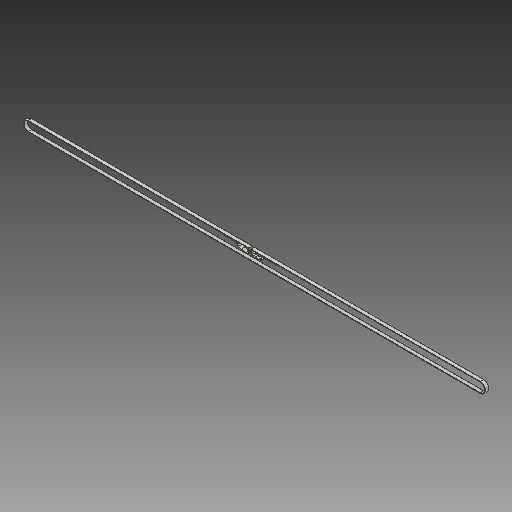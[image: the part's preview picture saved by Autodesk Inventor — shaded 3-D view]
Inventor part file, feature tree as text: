
AUTODESK INVENTOR PART (.ipt)
format: ipt  version: 2017 (Build 210142000, 142)  size: 181,760 bytes
history: native  units: mm
features: other x3, sketch x1
ambient origin geometry x8: Origin, YZ Plane, XZ Plane, XY Plane, X Axis, Y Axis, Z Axis, Center Point
bodies: Solid1 (feature_tree)
feature tree (4):
  other  "YBELT.ipt"
  other  "Solid1::YBELT.ipt"
  other  "TaggingFeature1"
  sketch  "Sketch1"  dims[d0=10.0mm]
